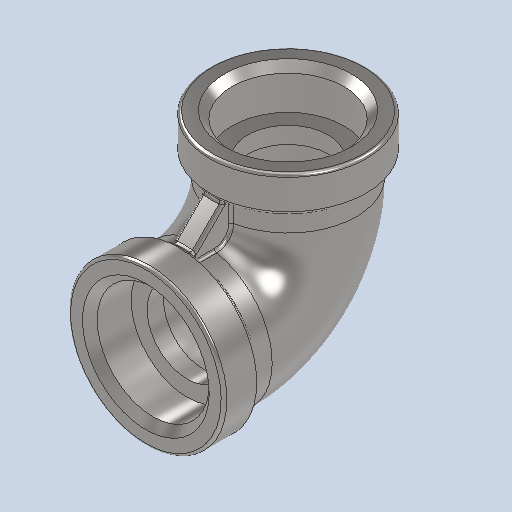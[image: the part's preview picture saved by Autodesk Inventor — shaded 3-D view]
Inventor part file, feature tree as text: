
AUTODESK INVENTOR PART (.ipt)
format: ipt  version: 2022 (Build 260153000, 153)  size: 364,544 bytes
history: native  units: in
note: dims shown in document units (in); Inventor stores cm internally (conversion verified against a paired STEP export)
features: fillet x1
ambient origin geometry x8: Origin, YZ Plane, XZ Plane, XY Plane, X Axis, Y Axis, Z Axis, Center Point
bodies: Solid1 (feature_tree)
feature tree (1):
  fillet  "Fillet5"  [1 undecoded]
note: 1 required parameter value undecoded (feature->parameter linkage not recoverable at this tier; creation-order binding heuristic only, values carry confidence <= 0.55)
